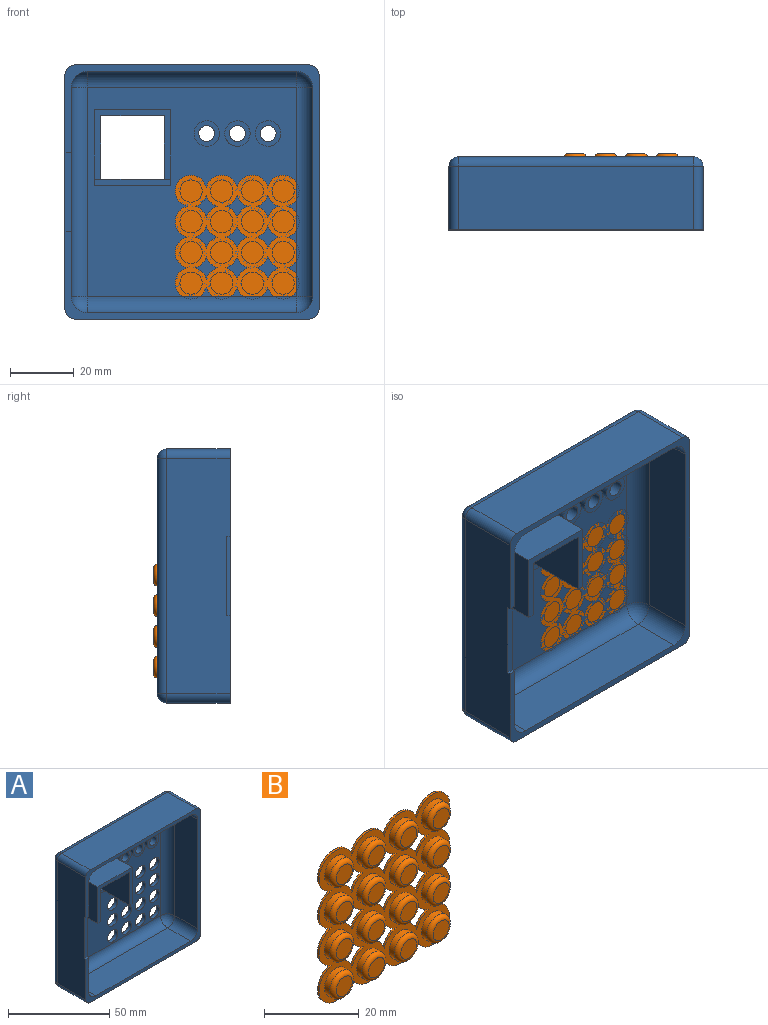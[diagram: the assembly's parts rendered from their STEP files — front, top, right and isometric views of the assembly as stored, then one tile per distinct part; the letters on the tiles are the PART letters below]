
ASSEMBLY  parts=2 mates=1
PART A: 75 faces, bbox 80x23x80 mm
  f0: plane 66x16mm, normal (1,0,0), area 1031mm2, adj f10,f25,f31,f34,f72,f73,f74
  f1: plane 66x66mm, normal (0,-1,0), area 3013.5mm2, adj f26,f27,f31,f32,f39,f40,f41,f42
  f2: plane 74x20mm, normal (1,0,0), area 1480mm2, adj f10,f16,f20,f22
  f3: plane 74x20mm, normal (0,0,1), area 1480mm2, adj f10,f13,f19,f22
  f4: plane 74x20mm, normal (-1,0,0), area 1455mm2, adj f10,f11,f13,f14,f72,f73,f74
  f5: plane 74x20mm, normal (0,0,-1), area 1480mm2, adj f10,f11,f15,f16
  f6: plane 74x74mm, normal (0,1,0), area 4401.3mm2, adj f14,f15,f19,f20,f35,f36,f37,f38
  f7: plane 66x16mm, normal (0,0,1), area 1056mm2, adj f10,f28,f32,f34
  f8: plane 66x16mm, normal (0,0,-1), area 1056mm2, adj f10,f23,f25,f26
  f9: plane 66x16mm, normal (-1,0,0), area 1056mm2, adj f10,f23,f27,f28
  f10: plane 80x80mm, normal (0,-1,0), area 587.7mm2, adj f0,f2,f3,f4,f5,f7,f8,f9
  f11: cylinder r=3mm len=20mm, axis (0,-1,0), area 94.2mm2, adj f4,f5,f10,f12
  f12: sphere r=3mm, area 14.1mm2, adj f11,f14,f15
  f13: cylinder r=3mm len=20mm, axis (0,1,0), area 94.2mm2, adj f3,f4,f10,f17
  f14: cylinder r=3mm len=74mm, axis (0,0,-1), area 348.7mm2, adj f4,f6,f12,f17
  f15: cylinder r=3mm len=74mm, axis (1,0,0), area 348.7mm2, adj f5,f6,f12,f18
  f16: cylinder r=3mm len=20mm, axis (0,1,0), area 94.2mm2, adj f2,f5,f10,f18
  f17: sphere r=3mm, area 14.1mm2, adj f13,f14,f19
  f18: sphere r=3mm, area 14.1mm2, adj f15,f16,f20
  f19: cylinder r=3mm len=74mm, axis (-1,0,0), area 348.7mm2, adj f3,f6,f17,f21
  f20: cylinder r=3mm len=74mm, axis (0,0,1), area 348.7mm2, adj f2,f6,f18,f21
  f21: sphere r=3mm, area 14.1mm2, adj f19,f20,f22
  f22: cylinder r=3mm len=20mm, axis (0,-1,0), area 94.2mm2, adj f2,f3,f10,f21
  f23: cylinder r=5mm len=16mm, axis (0,-1,0), area 125.7mm2, adj f8,f9,f10,f24
  f24: sphere r=5mm, area 39.3mm2, adj f23,f26,f27
  f25: cylinder r=5mm len=16mm, axis (0,1,0), area 125.7mm2, adj f0,f8,f10,f29
  f26: cylinder r=5mm len=66mm, axis (1,0,0), area 518.4mm2, adj f1,f8,f24,f29
  f27: cylinder r=5mm len=66mm, axis (0,0,-1), area 518.4mm2, adj f1,f9,f24,f30
  f28: cylinder r=5mm len=16mm, axis (0,1,0), area 125.7mm2, adj f7,f9,f10,f30
  f29: sphere r=5mm, area 39.3mm2, adj f25,f26,f31
  f30: sphere r=5mm, area 39.3mm2, adj f27,f28,f32
  f31: cylinder r=5mm len=66mm, axis (0,0,1), area 518.4mm2, adj f0,f1,f29,f33
  f32: cylinder r=5mm len=66mm, axis (-1,0,0), area 518.4mm2, adj f1,f7,f30,f33
  f33: sphere r=5mm, area 39.3mm2, adj f31,f32,f34
  f34: cylinder r=5mm len=16mm, axis (0,-1,0), area 125.7mm2, adj f0,f7,f10,f33
  f35: plane 22x20mm, normal (-1,0,0), area 440mm2, adj f6,f36,f38,f57,f60
  f36: plane 20x3mm, normal (0,0,1), area 60mm2, adj f6,f35,f37,f62
  f37: plane 22x20mm, normal (1,0,0), area 440mm2, adj f6,f36,f38,f56,f60
  f38: plane 22x20mm, normal (0,0,-1), area 440mm2, adj f6,f35,f37,f60
  f39: cylinder r=3.5mm len=7mm, axis (0,1,0), area 44mm2, adj f1,f6
  f40: cylinder r=3.5mm len=7mm, axis (0,1,0), area 44mm2, adj f1,f6
  f41: cylinder r=3.5mm len=7mm, axis (0,1,0), area 44mm2, adj f1,f6
  f42: cylinder r=3.5mm len=7mm, axis (0,1,0), area 44mm2, adj f1,f6
  f43: cylinder r=3.5mm len=7mm, axis (0,1,0), area 44mm2, adj f1,f6
  f44: cylinder r=3.5mm len=7mm, axis (0,1,0), area 44mm2, adj f1,f6
  f45: cylinder r=3.5mm len=7mm, axis (0,1,0), area 44mm2, adj f1,f6
  f46: cylinder r=3.5mm len=7mm, axis (0,1,0), area 44mm2, adj f1,f6
  f47: cylinder r=3.5mm len=7mm, axis (0,1,0), area 44mm2, adj f1,f6
  f48: cylinder r=3.5mm len=7mm, axis (0,1,0), area 44mm2, adj f1,f6
  f49: cylinder r=3.5mm len=7mm, axis (0,1,0), area 44mm2, adj f1,f6
  f50: cylinder r=3.5mm len=7mm, axis (0,1,0), area 44mm2, adj f1,f6
  f51: cylinder r=3.5mm len=7mm, axis (0,1,0), area 44mm2, adj f1,f6
  f52: cylinder r=3.5mm len=7mm, axis (0,1,0), area 44mm2, adj f1,f6
  f53: cylinder r=3.5mm len=7mm, axis (0,1,0), area 44mm2, adj f1,f6
  f54: cylinder r=3.5mm len=7mm, axis (0,1,0), area 44mm2, adj f1,f6
  f55: plane 24x20mm, normal (-1,0,0), area 442mm2, adj f1,f56,f59,f60,f61,f62
  f56: plane 19x2mm, normal (0,0,-1), area 38mm2, adj f37,f55,f60,f62
  f57: plane 19x2mm, normal (0,0,-1), area 38mm2, adj f35,f58,f60,f62
  f58: plane 24x20mm, normal (1,0,0), area 442mm2, adj f1,f57,f59,f60,f61,f62
  f59: plane 24x20mm, normal (0,0,1), area 480mm2, adj f1,f55,f58,f60
  f60: plane 24x22mm, normal (0,-1,0), area 128mm2, adj f35,f37,f38,f55,f56,f57,f58,f59
  f61: plane 24x1mm, normal (0,0,-1), area 24mm2, adj f1,f55,f58,f62
  f62: plane 24x2mm, normal (0,-1,0), area 48mm2, adj f36,f55,f56,f57,f58,f61
  f63: cylinder r=2.5mm len=6mm, axis (0,1,0), area 94.2mm2, adj f6,f71
  f64: cylinder r=2.5mm len=6mm, axis (0,1,0), area 94.2mm2, adj f6,f69
  f65: cylinder r=2.5mm len=6mm, axis (0,1,0), area 94.2mm2, adj f6,f67
  f66: cylinder r=4mm len=8mm, axis (0,1,0), area 100.5mm2, adj f1,f67
  f67: plane 8x8mm, normal (0,-1,0), area 30.6mm2, adj f65,f66
  f68: cylinder r=4mm len=8mm, axis (0,1,0), area 100.5mm2, adj f1,f69
  f69: plane 8x8mm, normal (0,-1,0), area 30.6mm2, adj f64,f68
  f70: cylinder r=4mm len=8mm, axis (0,1,0), area 100.5mm2, adj f1,f71
  f71: plane 8x8mm, normal (0,-1,0), area 30.6mm2, adj f63,f70
  f72: plane 2x1mm, normal (0,0,1), area 2mm2, adj f0,f4,f10,f74
  f73: plane 2x1mm, normal (0,0,-1), area 2mm2, adj f0,f4,f10,f74
  f74: plane 25x2mm, normal (0,-1,0), area 50mm2, adj f0,f4,f72,f73
PART B: 98 faces, bbox 39x3x39 mm
  f0: cylinder r=3.4mm len=6.8mm, axis (0,1,0), area 32mm2, adj f2,f46
  f1: plane 4.8x4.8mm, normal (0,-1,0), area 18.1mm2, adj f2
  f2: torus R=2.4mm, axis (0,-1,0), area 30mm2, adj f0,f1
  f3: cylinder r=3.4mm len=6.8mm, axis (0,1,0), area 32mm2, adj f5,f46
  f4: plane 4.8x4.8mm, normal (0,-1,0), area 18.1mm2, adj f5
  f5: torus R=2.4mm, axis (0,-1,0), area 30mm2, adj f3,f4
  f6: cylinder r=3.4mm len=6.8mm, axis (0,1,0), area 32mm2, adj f8,f46
  f7: plane 4.8x4.8mm, normal (0,-1,0), area 18.1mm2, adj f8
  f8: torus R=2.4mm, axis (0,-1,0), area 30mm2, adj f6,f7
  f9: cylinder r=3.4mm len=6.8mm, axis (0,1,0), area 32mm2, adj f11,f46
  f10: plane 4.8x4.8mm, normal (0,-1,0), area 18.1mm2, adj f11
  f11: torus R=2.4mm, axis (0,-1,0), area 30mm2, adj f9,f10
  f12: cylinder r=3.4mm len=6.8mm, axis (0,1,0), area 32mm2, adj f14,f46
  f13: plane 4.8x4.8mm, normal (0,-1,0), area 18.1mm2, adj f14
  f14: torus R=2.4mm, axis (0,-1,0), area 30mm2, adj f12,f13
  f15: cylinder r=3.4mm len=6.8mm, axis (0,1,0), area 32mm2, adj f17,f46
  f16: plane 4.8x4.8mm, normal (0,-1,0), area 18.1mm2, adj f17
  f17: torus R=2.4mm, axis (0,-1,0), area 30mm2, adj f15,f16
  f18: cylinder r=3.4mm len=6.8mm, axis (0,1,0), area 32mm2, adj f20,f46
  f19: plane 4.8x4.8mm, normal (0,-1,0), area 18.1mm2, adj f20
  f20: torus R=2.4mm, axis (0,-1,0), area 30mm2, adj f18,f19
  f21: cylinder r=5mm len=9.67mm, axis (0,-1,0), area 6.6mm2, adj f31,f45,f46,f63
  f22: cylinder r=5mm len=3.56mm, axis (0,-1,0), area 2.6mm2, adj f23,f41,f45,f46
  f23: cylinder r=5mm len=3.56mm, axis (0,-1,0), area 2.6mm2, adj f22,f24,f45,f46
  f24: cylinder r=5mm len=3.56mm, axis (0,-1,0), area 2.6mm2, adj f23,f41,f45,f46
  f25: cylinder r=5mm len=3.56mm, axis (0,-1,0), area 2.6mm2, adj f26,f42,f45,f46
  f26: cylinder r=5mm len=3.56mm, axis (0,-1,0), area 2.6mm2, adj f25,f27,f45,f46
  f27: cylinder r=5mm len=3.56mm, axis (0,-1,0), area 2.6mm2, adj f26,f42,f45,f46
  f28: cylinder r=5mm len=9.84mm, axis (0,-1,0), area 10.5mm2, adj f29,f43,f45,f46
  f29: cylinder r=5mm len=9.67mm, axis (0,-1,0), area 6.6mm2, adj f28,f30,f45,f46
  f30: cylinder r=5mm len=9.67mm, axis (0,-1,0), area 6.6mm2, adj f29,f31,f45,f46
  f31: cylinder r=5mm len=9.84mm, axis (0,-1,0), area 10.5mm2, adj f21,f30,f45,f46
  f32: cylinder r=5mm len=3.56mm, axis (0,-1,0), area 2.6mm2, adj f33,f45,f46,f62
  f33: cylinder r=5mm len=3.56mm, axis (0,-1,0), area 2.6mm2, adj f32,f45,f46,f49
  f34: cylinder r=5mm len=3.54mm, axis (0,-1,0), area 2.6mm2, adj f35,f45,f46,f61
  f35: cylinder r=5mm len=3.54mm, axis (0,-1,0), area 2.6mm2, adj f34,f45,f46,f48
  f36: cylinder r=5mm len=3.56mm, axis (0,-1,0), area 2.6mm2, adj f37,f45,f46,f60
  f37: cylinder r=5mm len=3.56mm, axis (0,-1,0), area 2.6mm2, adj f36,f45,f46,f47
  f38: cylinder r=5mm len=3.56mm, axis (0,-1,0), area 2.6mm2, adj f39,f44,f45,f46
  f39: cylinder r=5mm len=3.56mm, axis (0,-1,0), area 2.6mm2, adj f38,f40,f45,f46
  f40: cylinder r=5mm len=3.56mm, axis (0,-1,0), area 2.6mm2, adj f39,f44,f45,f46
  f41: cylinder r=5mm len=3.56mm, axis (0,-1,0), area 2.6mm2, adj f22,f24,f45,f46
  f42: cylinder r=5mm len=3.56mm, axis (0,-1,0), area 2.6mm2, adj f25,f27,f45,f46
  f43: cylinder r=5mm len=9.67mm, axis (0,-1,0), area 6.6mm2, adj f28,f45,f46,f59
  f44: cylinder r=5mm len=3.56mm, axis (0,-1,0), area 2.6mm2, adj f38,f40,f45,f46
  f45: plane 39x39mm, normal (0,1,0), area 1242.9mm2, adj f21,f22,f23,f24,f25,f26,f27,f28
  f46: plane 39x39mm, normal (0,-1,0), area 661.9mm2, adj f0,f3,f6,f9,f12,f15,f18,f21
  f47: cylinder r=5mm len=3.56mm, axis (0,-1,0), area 2.6mm2, adj f37,f45,f46,f60
  f48: cylinder r=5mm len=3.54mm, axis (0,-1,0), area 2.6mm2, adj f35,f45,f46,f61
  f49: cylinder r=5mm len=3.56mm, axis (0,-1,0), area 2.6mm2, adj f33,f45,f46,f62
  f50: cylinder r=5mm len=3.56mm, axis (0,-1,0), area 2.6mm2, adj f45,f46,f51,f67
  f51: cylinder r=5mm len=3.56mm, axis (0,-1,0), area 2.6mm2, adj f45,f46,f50,f52
  f52: cylinder r=5mm len=3.56mm, axis (0,-1,0), area 2.6mm2, adj f45,f46,f51,f67
  f53: cylinder r=5mm len=3.56mm, axis (0,-1,0), area 2.6mm2, adj f45,f46,f54,f68
  f54: cylinder r=5mm len=3.56mm, axis (0,-1,0), area 2.6mm2, adj f45,f46,f53,f55
  f55: cylinder r=5mm len=3.56mm, axis (0,-1,0), area 2.6mm2, adj f45,f46,f54,f68
  f56: cylinder r=5mm len=3.56mm, axis (0,-1,0), area 2.6mm2, adj f45,f46,f57,f69
  f57: cylinder r=5mm len=3.56mm, axis (0,-1,0), area 2.6mm2, adj f45,f46,f56,f58
  f58: cylinder r=5mm len=3.56mm, axis (0,-1,0), area 2.6mm2, adj f45,f46,f57,f69
  f59: cylinder r=5mm len=9.67mm, axis (0,-1,0), area 6.6mm2, adj f43,f45,f46,f70
  f60: cylinder r=5mm len=3.56mm, axis (0,-1,0), area 2.6mm2, adj f36,f45,f46,f47
  f61: cylinder r=5mm len=3.54mm, axis (0,-1,0), area 2.6mm2, adj f34,f45,f46,f48
  f62: cylinder r=5mm len=3.56mm, axis (0,-1,0), area 2.6mm2, adj f32,f45,f46,f49
  f63: cylinder r=5mm len=9.67mm, axis (0,-1,0), area 6.6mm2, adj f21,f45,f46,f64
  f64: cylinder r=5mm len=9.84mm, axis (0,-1,0), area 10.5mm2, adj f45,f46,f63,f65
  f65: cylinder r=5mm len=9.67mm, axis (0,-1,0), area 6.6mm2, adj f45,f46,f64,f66
  f66: cylinder r=5mm len=9.67mm, axis (0,-1,0), area 6.6mm2, adj f45,f46,f65,f70
  f67: cylinder r=5mm len=3.56mm, axis (0,-1,0), area 2.6mm2, adj f45,f46,f50,f52
  f68: cylinder r=5mm len=3.56mm, axis (0,-1,0), area 2.6mm2, adj f45,f46,f53,f55
  f69: cylinder r=5mm len=3.56mm, axis (0,-1,0), area 2.6mm2, adj f45,f46,f56,f58
  f70: cylinder r=5mm len=9.84mm, axis (0,-1,0), area 10.5mm2, adj f45,f46,f59,f66
  f71: cylinder r=3.4mm len=6.8mm, axis (0,-1,0), area 32mm2, adj f46,f73
  f72: plane 4.8x4.8mm, normal (0,-1,0), area 18.1mm2, adj f73
  f73: torus R=2.4mm, axis (0,-1,0), area 30mm2, adj f71,f72
  f74: cylinder r=3.4mm len=6.8mm, axis (0,-1,0), area 32mm2, adj f46,f76
  f75: plane 4.8x4.8mm, normal (0,-1,0), area 18.1mm2, adj f76
  f76: torus R=2.4mm, axis (0,-1,0), area 30mm2, adj f74,f75
  f77: cylinder r=3.4mm len=6.8mm, axis (0,-1,0), area 32mm2, adj f46,f79
  f78: plane 4.8x4.8mm, normal (0,-1,0), area 18.1mm2, adj f79
  f79: torus R=2.4mm, axis (0,-1,0), area 30mm2, adj f77,f78
  f80: cylinder r=3.4mm len=6.8mm, axis (0,-1,0), area 32mm2, adj f46,f82
  f81: plane 4.8x4.8mm, normal (0,-1,0), area 18.1mm2, adj f82
  f82: torus R=2.4mm, axis (0,-1,0), area 30mm2, adj f80,f81
  f83: cylinder r=3.4mm len=6.8mm, axis (0,-1,0), area 32mm2, adj f46,f85
  f84: plane 4.8x4.8mm, normal (0,-1,0), area 18.1mm2, adj f85
  f85: torus R=2.4mm, axis (0,-1,0), area 30mm2, adj f83,f84
  f86: cylinder r=3.4mm len=6.8mm, axis (0,-1,0), area 32mm2, adj f46,f88
  f87: plane 4.8x4.8mm, normal (0,-1,0), area 18.1mm2, adj f88
  f88: torus R=2.4mm, axis (0,-1,0), area 30mm2, adj f86,f87
  f89: cylinder r=3.4mm len=6.8mm, axis (0,-1,0), area 32mm2, adj f46,f91
  f90: plane 4.8x4.8mm, normal (0,-1,0), area 18.1mm2, adj f91
  f91: torus R=2.4mm, axis (0,-1,0), area 30mm2, adj f89,f90
  f92: cylinder r=3.4mm len=6.8mm, axis (0,-1,0), area 32mm2, adj f46,f94
  f93: plane 4.8x4.8mm, normal (0,-1,0), area 18.1mm2, adj f94
  f94: torus R=2.4mm, axis (0,-1,0), area 30mm2, adj f92,f93
  f95: cylinder r=3.4mm len=6.8mm, axis (0,-1,0), area 32mm2, adj f46,f97
  f96: plane 4.8x4.8mm, normal (0,-1,0), area 18.1mm2, adj f97
  f97: torus R=2.4mm, axis (0,-1,0), area 30mm2, adj f95,f96
PLACE A t=(-91.19,-3.37,0.5)mm
PLACE B rot(axis=(0,0,1),180deg) t=(-91.49,-4.87,-28.2)mm
MATE planar B.f12 <-> A.f39  axis (0,1,0) through (-62.49,-3.37,0.8)mm
